# Revit family: BVN_BSKF-R
name_source: partatom
category: Mechanical Equipment
units: mm (PartAtom-declared; Revit-internal decimal feet)

## family parameters
Always vertical = Yes
Cut with Voids When Loaded = No
OmniClass Number = 23.75.00.00
OmniClass Title = Climate Control (HVAC)
Part Type = Breaks Into
Room Calculation Point = No
Round Connector Dimension = Use Diameter
Shared = No
Work Plane-Based = No

## types (15) — shared parameters
Corners = 20 mm  [stored 0.0656168 ft]
Description = Duct Fan
Frequency = 50 Hz
Insulation Class = F
Manufacturer = Bahçıvan Elektrik Motor San. ve Tic. Ltd. Şti.
Material = <By Category>
Model = BSKF-R
Protection Class = 55
Sac = -2 mm  [stored -0.00656168 ft]
URL = http://www.bahcivanmotor.com.tr

## per-type parameters (varying)
| type | 150 | 180 | A | Air Flow | B | C | Capacitor(uF) | Current | D | E | F | G | Power | Sound Pressure Level dB(A) | Speed ( d/d ) | Voltage | Weight | motor_x | motor_y |
| BSKF-R 200-4 T | Yes | No | 200 mm  [stored 0.656168 ft] | 1000.0 m³/h | 400 mm  [stored 1.31234 ft] | 500 mm  [stored 1.64042 ft] | 0 | 1 A | 420 mm  [stored 1.37795 ft] | 220 mm  [stored 0.721785 ft] | 450 mm  [stored 1.47638 ft] | 250 mm  [stored 0.82021 ft] | 250 W | 53 | 1380 | 380 V | 22.00 kg | 50 mm  [stored 0.164042 ft] | 30 mm  [stored 0.0984252 ft] |
| BSKF-R 355-4 T | No | Yes | 400 mm  [stored 1.31234 ft] | 8000.0 m³/h | 700 mm  [stored 2.29659 ft] | 780 mm  [stored 2.55906 ft] | 0 | 5 A | 720 mm  [stored 2.3622 ft] | 420 mm  [stored 1.37795 ft] | 750 mm  [stored 2.46063 ft] | 450 mm  [stored 1.47638 ft] | 2200 W | 64 | 1420 | 380 V | 85.00 kg | 100 mm  [stored 0.328084 ft] | 70 mm  [stored 0.229659 ft] |
| BSKF-R 400-6 T | No | Yes | 500 mm  [stored 1.64042 ft] | 6000.0 m³/h | 800 mm  [stored 2.62467 ft] | 880 mm  [stored 2.88714 ft] | 0 | 4 A | 820 mm  [stored 2.69029 ft] | 520 mm  [stored 1.70604 ft] | 850 mm  [stored 2.78871 ft] | 550 mm | 1500 W | 55 | 945 | 380 V | 92.00 kg | 100 mm  [stored 0.328084 ft] | 80 mm  [stored 0.262467 ft] |
| BSKF-R 450-6 T | No | Yes | 500 mm  [stored 1.64042 ft] | 7500.0 m³/h | 1000 mm  [stored 3.28084 ft] | 980 mm  [stored 3.21522 ft] | 0 | 5 A | 1020 mm  [stored 3.34646 ft] | 520 mm  [stored 1.70604 ft] | 1050 mm | 550 mm | 2200 W | 58 | 950 | 380 V | 120.00 kg | 100 mm  [stored 0.328084 ft] | 80 mm  [stored 0.262467 ft] |
| BSKF-R 225-4 T | Yes | No | 250 mm  [stored 0.82021 ft] | 1673.0 m³/h | 500 mm  [stored 1.64042 ft] | 560 mm  [stored 1.83727 ft] | 0 | 1 A | 520 mm  [stored 1.70604 ft] | 270 mm  [stored 0.885827 ft] | 550 mm | 300 mm | 370 W | 55 | 1390 | 380 V | 35.00 kg | 70 mm  [stored 0.229659 ft] | 50 mm  [stored 0.164042 ft] |
| BSKF-R 250-4 T | Yes | No | 300 mm | 1740.0 m³/h | 500 mm  [stored 1.64042 ft] | 560 mm  [stored 1.83727 ft] | 0 | 2 A | 520 mm  [stored 1.70604 ft] | 320 mm  [stored 1.04987 ft] | 550 mm | 350 mm  [stored 1.14829 ft] | 550 W | 55 | 1365 | 380 V | 40.00 kg | 70 mm  [stored 0.229659 ft] | 30 mm  [stored 0.0984252 ft] |
| BSKF-R 280-4 T | Yes | No | 300 mm | 2942.0 m³/h | 600 mm | 710 mm | 0 | 2 A | 620 mm  [stored 2.03412 ft] | 320 mm  [stored 1.04987 ft] | 650 mm  [stored 2.13255 ft] | 350 mm  [stored 1.14829 ft] | 750 W | 60 | 1405 | 380 V | 43.00 kg | 100 mm  [stored 0.328084 ft] | 50 mm  [stored 0.164042 ft] |
| BSKF-R 315-4 T | Yes | No | 350 mm  [stored 1.14829 ft] | 4050.0 m³/h | 600 mm | 710 mm | 0 | 4 A | 620 mm  [stored 2.03412 ft] | 370 mm  [stored 1.21391 ft] | 650 mm  [stored 2.13255 ft] | 400 mm  [stored 1.31234 ft] | 1500 W | 62 | 1410 | 380 V | 55.00 kg | 100 mm  [stored 0.328084 ft] | 60 mm  [stored 0.19685 ft] |
| BSKF-R 355-6 T | No | Yes | 400 mm  [stored 1.31234 ft] | 5200.0 m³/h | 700 mm  [stored 2.29659 ft] | 780 mm  [stored 2.55906 ft] | 0 | 3 A | 720 mm  [stored 2.3622 ft] | 420 mm  [stored 1.37795 ft] | 750 mm  [stored 2.46063 ft] | 450 mm  [stored 1.47638 ft] | 1100 W | 53 | 930 | 380 V | 85.00 kg | 100 mm  [stored 0.328084 ft] | 70 mm  [stored 0.229659 ft] |
| BSKF-R 200-4 M | Yes | Yes | 200 mm  [stored 0.656168 ft] | 1000.0 m³/h | 400 mm  [stored 1.31234 ft] | 500 mm  [stored 1.64042 ft] | 10 | 2 A | 420 mm  [stored 1.37795 ft] | 220 mm  [stored 0.721785 ft] | 450 mm  [stored 1.47638 ft] | 250 mm  [stored 0.82021 ft] | 250 W | 53 | 1390 | 230 V | 22.00 kg | 50 mm  [stored 0.164042 ft] | 30 mm  [stored 0.0984252 ft] |
| BSKF-R 225-4 M | Yes | No | 250 mm  [stored 0.82021 ft] | 1673.0 m³/h | 500 mm  [stored 1.64042 ft] | 560 mm  [stored 1.83727 ft] | 15 | 3 A | 520 mm  [stored 1.70604 ft] | 270 mm  [stored 0.885827 ft] | 550 mm | 300 mm | 370 W | 55 | 1400 | 230 V | 35.00 kg | 70 mm  [stored 0.229659 ft] | 50 mm  [stored 0.164042 ft] |
| BSKF-R 250-4 M | Yes | No | 300 mm | 1740.0 m³/h | 500 mm  [stored 1.64042 ft] | 560 mm  [stored 1.83727 ft] | 20 | 5 A | 520 mm  [stored 1.70604 ft] | 320 mm  [stored 1.04987 ft] | 550 mm | 350 mm  [stored 1.14829 ft] | 550 W | 55 | 1365 | 230 V | 40.00 kg | 70 mm  [stored 0.229659 ft] | 30 mm  [stored 0.0984252 ft] |
| BSKF-R 280-4 M | Yes | No | 300 mm | 2942.0 m³/h | 600 mm | 710 mm | 30 | 5 A | 620 mm  [stored 2.03412 ft] | 320 mm  [stored 1.04987 ft] | 650 mm  [stored 2.13255 ft] | 350 mm  [stored 1.14829 ft] | 750 W | 60 | 1405 | 230 V | 43.00 kg | 100 mm  [stored 0.328084 ft] | 50 mm  [stored 0.164042 ft] |
| BSKF-R 315-4 M | Yes | No | 350 mm  [stored 1.14829 ft] | 4050.0 m³/h | 600 mm | 710 mm | 50 | 9 A | 620 mm  [stored 2.03412 ft] | 370 mm  [stored 1.21391 ft] | 650 mm  [stored 2.13255 ft] | 400 mm  [stored 1.31234 ft] | 1500 W | 62 | 1410 | 230 V | 55.00 kg | 100 mm  [stored 0.328084 ft] | 60 mm  [stored 0.19685 ft] |
| BSKF-R 355-4 M | No | Yes | 400 mm  [stored 1.31234 ft] | 8000.0 m³/h | 700 mm  [stored 2.29659 ft] | 780 mm  [stored 2.55906 ft] | 50 | 14 A | 720 mm  [stored 2.3622 ft] | 420 mm  [stored 1.37795 ft] | 750 mm  [stored 2.46063 ft] | 450 mm  [stored 1.47638 ft] | 2200 W | 64 | 1430 | 230 V | 85.00 kg | 100 mm  [stored 0.328084 ft] | 70 mm  [stored 0.229659 ft] |

note: [stored X ft] marks values corroborated as IEEE doubles in the binary element streams (Revit-internal decimal feet)

## geometry (parser evidence)
native form markers: Sweep x2
no freeform markers — native parametric forms only
